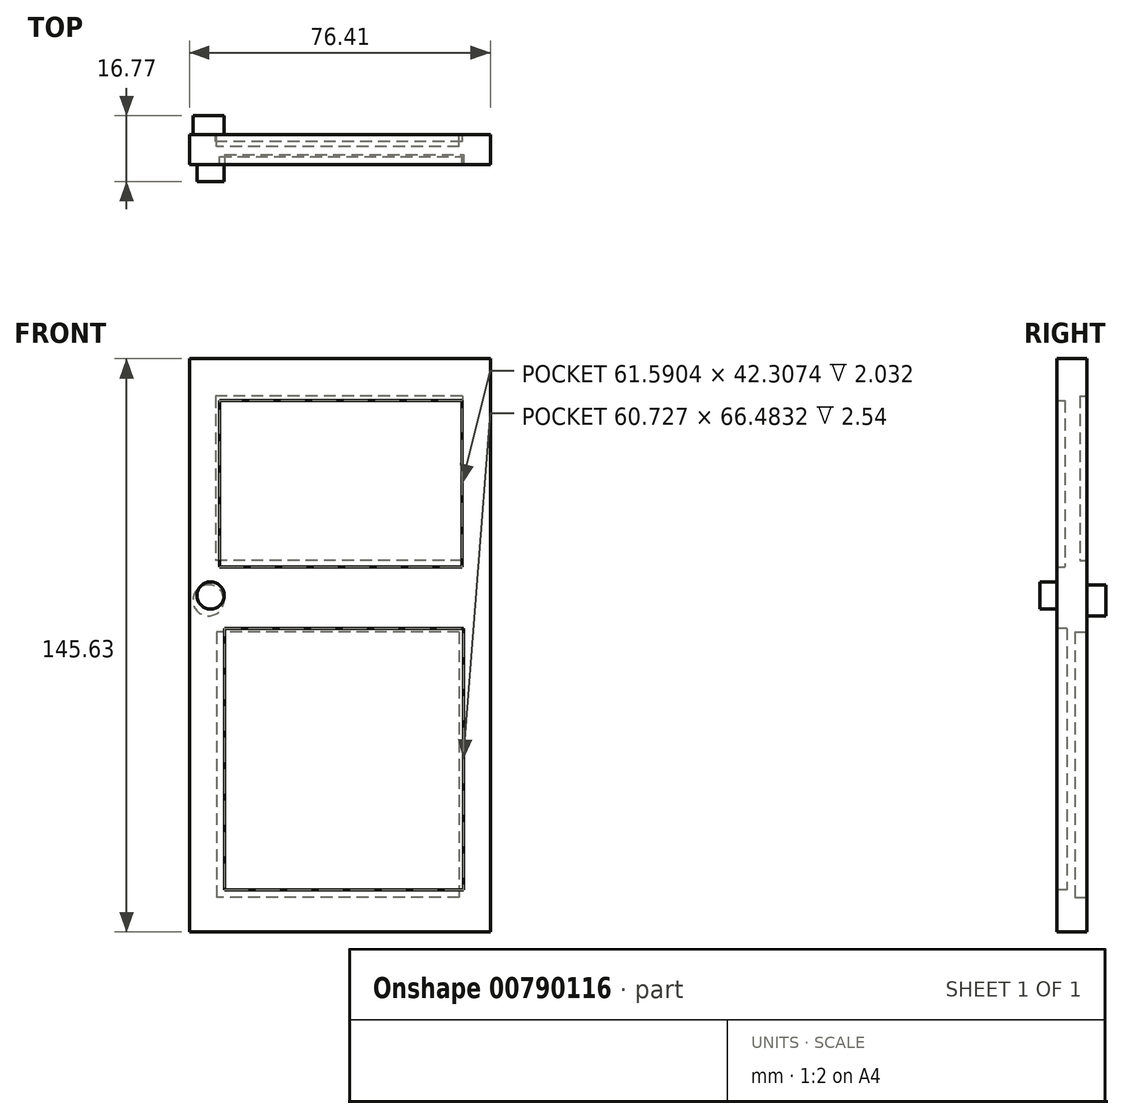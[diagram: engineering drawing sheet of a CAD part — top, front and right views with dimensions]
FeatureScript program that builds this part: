
annotation { "Feature Type Name" : "Feature", "Feature Type Description" : "" }
export const myFeature = defineFeature(function(context is Context, id is Id, definition is map)
    precondition{}
    {
        {
            var Q0;
            Q0=qCreatedBy(makeId("Front.planeOp"),FACE);
            var sketch = newSketch(context, id + "F0", { "sketchPlane" : qUnion([Q0])});
            skLineSegment(sketch, "E0.bottom", {"start": v(0, 72.67) * mm, "end": v(76.41, 72.67) * mm});
            skLineSegment(sketch, "E0.top", {"start": v(0, -72.96) * mm, "end": v(76.41, -72.96) * mm});
            skLineSegment(sketch, "E0.left", {"start": v(0, 72.67) * mm, "end": v(0, -72.96) * mm});
            skLineSegment(sketch, "E0.right", {"start": v(76.41, 72.67) * mm, "end": v(76.41, -72.96) * mm});
            skSolve(sketch);
        }
        {
            var Q0;
            Q0=makeQuery(id+"F0.imprint","IMPRINT",FACE,{"disambiguationData":[TD([[makeQuery(id+"F0.imprint","IMPRINT",EDGE,{"derivedFrom":sQuery(id+"F0.wireOp",EDGE,"E0.bottom")}),-1.0]])]});
            var sketch = newSketch(context, id + "F1", { "sketchPlane" : qUnion([Q0])});
            skLineSegment(sketch, "E1.bottom", {"start": v(7.63, 62.02) * mm, "end": v(69.22, 62.02) * mm});
            skLineSegment(sketch, "E1.top", {"start": v(7.63, 19.71) * mm, "end": v(69.22, 19.71) * mm});
            skLineSegment(sketch, "E1.left", {"start": v(7.63, 62.02) * mm, "end": v(7.63, 19.71) * mm});
            skLineSegment(sketch, "E1.right", {"start": v(69.22, 62.02) * mm, "end": v(69.22, 19.71) * mm});
            skSolve(sketch);
        }
        {
            var Q0;
            Q0=makeQuery(id+"F0.imprint","IMPRINT",FACE,{"disambiguationData":[TD([[makeQuery(id+"F0.imprint","IMPRINT",EDGE,{"derivedFrom":sQuery(id+"F0.wireOp",EDGE,"E0.bottom")}),-1.0]])]});
            var sketch = newSketch(context, id + "F2", { "sketchPlane" : qUnion([Q0])});
            skCircle(sketch, "E2", {"center": v(5.32, 12.52) * mm, "radius": 3.47 * mm});
            skSolve(sketch);
        }
        {
            var Q0;
            Q0 = qSketchRegion(id + "F2", true);
            extrude(context, id + "F3", {"entities" : qUnion([Q0]), "depth" : 8.13 * mm, "offsetDistance" : 25.4 * mm});
        }
        {
            var Q0;
            Q0=makeQuery(id+"F1.imprint","IMPRINT",FACE,{"disambiguationData":[TD([[makeQuery(id+"F1.imprint","IMPRINT",EDGE,{"derivedFrom":sQuery(id+"F1.wireOp",EDGE,"E1.bottom")}),1.0]])]});
            extrude(context, id + "F4", {"entities" : qUnion([Q0]), "operationType" : NewBodyOperationType.ADD, "depth" : 3.8 * mm, "offsetDistance" : 25.4 * mm});
        }
        {
            var Q0;
            Q0 = qSketchRegion(id + "F1", true);
            extrude(context, id + "F5", {"entities" : qUnion([Q0]), "operationType" : NewBodyOperationType.ADD, "depth" : 1.78 * mm, "offsetDistance" : 25.4 * mm});
        }
        {
            var Q0;
            Q0=makeQuery(id+"F4.opExtrude","CAP_FACE",FACE,{"disambiguationData":[OSD([sQuery(id+"F0.wireOp",EDGE,"E0.bottom"),sQuery(id+"F0.wireOp",EDGE,"E0.top"),sQuery(id+"F0.wireOp",EDGE,"E0.left"),sQuery(id+"F0.wireOp",EDGE,"E0.right"),sQuery(id+"F1.wireOp",EDGE,"E1.bottom"),sQuery(id+"F1.wireOp",EDGE,"E1.top"),sQuery(id+"F1.wireOp",EDGE,"E1.left"),sQuery(id+"F1.wireOp",EDGE,"E1.right")])],"isStart":false});
            var sketch = newSketch(context, id + "F6", { "sketchPlane" : qUnion([Q0])});
            skLineSegment(sketch, "E3.bottom", {"start": v(8.88, 4.17) * mm, "end": v(69.61, 4.17) * mm});
            skLineSegment(sketch, "E3.top", {"start": v(8.88, -62.3) * mm, "end": v(69.61, -62.3) * mm});
            skLineSegment(sketch, "E3.left", {"start": v(8.88, 4.17) * mm, "end": v(8.88, -62.3) * mm});
            skLineSegment(sketch, "E3.right", {"start": v(69.61, 4.17) * mm, "end": v(69.61, -62.3) * mm});
            skSolve(sketch);
        }
        {
            var Q0;
            Q0=makeQuery(id+"F6.imprint","IMPRINT",FACE,{"disambiguationData":[TD([[makeQuery(id+"F6.imprint","IMPRINT",EDGE,{"derivedFrom":sQuery(id+"F6.wireOp",EDGE,"E3.bottom")}),-1.0]])]});
            extrude(context, id + "F7", {"entities" : qUnion([Q0]), "operationType" : NewBodyOperationType.REMOVE, "oppositeDirection" : true, "depth" : 2.54 * mm, "offsetDistance" : 25.4 * mm});
        }
        {
            var Q0;
            Q0=makeQuery(id+"F0.imprint","IMPRINT",FACE,{"disambiguationData":[TD([[makeQuery(id+"F0.imprint","IMPRINT",EDGE,{"derivedFrom":sQuery(id+"F0.wireOp",EDGE,"E0.bottom")}),-1.0]])]});
            extrude(context, id + "F8", {"entities" : qUnion([Q0]), "operationType" : NewBodyOperationType.ADD, "oppositeDirection" : true, "depth" : 3.8 * mm, "offsetDistance" : 25.4 * mm});
        }
        {
            var Q0;
            Q0=makeQuery(id+"F8.opExtrude","CAP_FACE",FACE,{"disambiguationData":[OSD([sQuery(id+"F0.wireOp",EDGE,"E0.bottom"),sQuery(id+"F0.wireOp",EDGE,"E0.top"),sQuery(id+"F0.wireOp",EDGE,"E0.left"),sQuery(id+"F0.wireOp",EDGE,"E0.right")])],"isStart":false});
            var sketch = newSketch(context, id + "F9", { "sketchPlane" : qUnion([Q0])});
            skSolve(sketch);
        }
        {
            var Q0;
            Q0=makeQuery(id+"F9.imprint","IMPRINT",FACE,{"disambiguationData":[TD([[makeQuery(id+"F9.imprint","IMPRINT",EDGE,{"derivedFrom":makeQuery(id+"F8.opExtrude","CAP_EDGE",EDGE,{"disambiguationData":[OSD([sQuery(id+"F0.wireOp",EDGE,"E0.bottom")])],"isStart":false})}),1.0]])]});
            var sketch = newSketch(context, id + "F10", { "sketchPlane" : qUnion([Q0])});
            skLineSegment(sketch, "E4.bottom", {"start": v(-69.32, 63.17) * mm, "end": v(-6.58, 63.17) * mm});
            skLineSegment(sketch, "E4.top", {"start": v(-69.32, 21.44) * mm, "end": v(-6.58, 21.44) * mm});
            skLineSegment(sketch, "E4.left", {"start": v(-69.32, 63.17) * mm, "end": v(-69.32, 21.44) * mm});
            skLineSegment(sketch, "E4.right", {"start": v(-6.58, 63.17) * mm, "end": v(-6.58, 21.44) * mm});
            skSolve(sketch);
        }
        {
            var Q0;
            Q0=makeQuery(id+"F10.imprint","IMPRINT",FACE,{"disambiguationData":[TD([[makeQuery(id+"F10.imprint","IMPRINT",EDGE,{"derivedFrom":sQuery(id+"F10.wireOp",EDGE,"E4.bottom")}),-1.0]])]});
            extrude(context, id + "F11", {"entities" : qUnion([Q0]), "operationType" : NewBodyOperationType.REMOVE, "oppositeDirection" : true, "depth" : 1.78 * mm, "offsetDistance" : 25.4 * mm});
        }
        {
            var Q0;
            Q0=makeQuery(id+"F9.imprint","IMPRINT",FACE,{"disambiguationData":[TD([[makeQuery(id+"F9.imprint","IMPRINT",EDGE,{"derivedFrom":makeQuery(id+"F8.opExtrude","CAP_EDGE",EDGE,{"disambiguationData":[OSD([sQuery(id+"F0.wireOp",EDGE,"E0.bottom")])],"isStart":false})}),1.0]])]});
            var sketch = newSketch(context, id + "F12", { "sketchPlane" : qUnion([Q0])});
            skLineSegment(sketch, "E5.bottom", {"start": v(-68.47, 3.2) * mm, "end": v(-6.86, 3.2) * mm});
            skLineSegment(sketch, "E5.top", {"start": v(-68.47, -64.2) * mm, "end": v(-6.86, -64.2) * mm});
            skLineSegment(sketch, "E5.left", {"start": v(-68.47, 3.2) * mm, "end": v(-68.47, -64.2) * mm});
            skLineSegment(sketch, "E5.right", {"start": v(-6.86, 3.2) * mm, "end": v(-6.86, -64.2) * mm});
            skLineSegment(sketch, "E6.bottom", {"start": v(-6.86, -64.2) * mm, "end": v(90.06, -64.2) * mm});
            skLineSegment(sketch, "E6.top", {"start": v(-6.86, -37.78) * mm, "end": v(90.06, -37.78) * mm});
            skLineSegment(sketch, "E6.left", {"start": v(-6.86, -64.2) * mm, "end": v(-6.86, -37.78) * mm});
            skLineSegment(sketch, "E6.right", {"start": v(90.06, -64.2) * mm, "end": v(90.06, -37.78) * mm});
            skSolve(sketch);
        }
        {
            var Q0;
            Q0=makeQuery(id+"F12.imprint","IMPRINT",FACE,{"disambiguationData":[TD([[makeQuery(id+"F12.imprint","IMPRINT",EDGE,{"derivedFrom":sQuery(id+"F12.wireOp",EDGE,"E5.bottom")}),-1.0]])]});
            extrude(context, id + "F13", {"entities" : qUnion([Q0]), "operationType" : NewBodyOperationType.REMOVE, "oppositeDirection" : true, "depth" : 3.05 * mm, "offsetDistance" : 25.4 * mm});
        }
        {
            var Q0;
            Q0=makeQuery(id+"F9.imprint","IMPRINT",FACE,{"disambiguationData":[TD([[makeQuery(id+"F9.imprint","IMPRINT",EDGE,{"derivedFrom":makeQuery(id+"F8.opExtrude","CAP_EDGE",EDGE,{"disambiguationData":[OSD([sQuery(id+"F0.wireOp",EDGE,"E0.bottom")])],"isStart":false})}),1.0]])]});
            var sketch = newSketch(context, id + "F14", { "sketchPlane" : qUnion([Q0])});
            skCircle(sketch, "E7", {"center": v(-4.8, 11.28) * mm, "radius": 3.95 * mm});
            skSolve(sketch);
        }
        {
            var Q0;
            Q0 = qSketchRegion(id + "F14", true);
            extrude(context, id + "F15", {"entities" : qUnion([Q0]), "operationType" : NewBodyOperationType.ADD, "depth" : 4.83 * mm, "offsetDistance" : 25.4 * mm});
        }
    });
